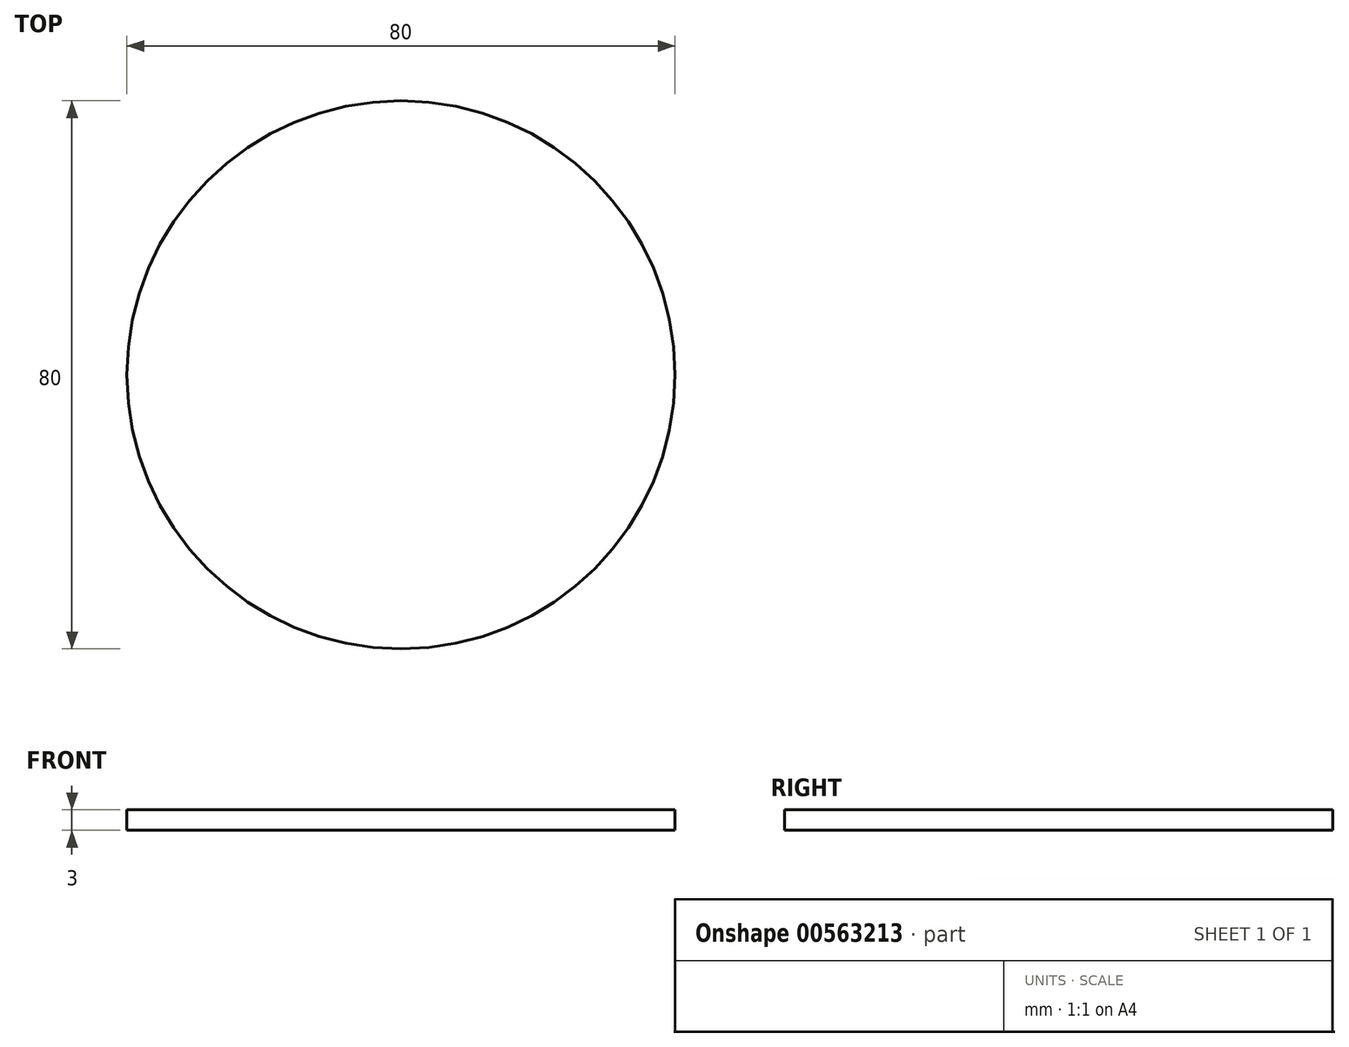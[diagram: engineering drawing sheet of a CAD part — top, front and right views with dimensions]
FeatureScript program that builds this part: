
annotation { "Feature Type Name" : "Feature", "Feature Type Description" : "" }
export const myFeature = defineFeature(function(context is Context, id is Id, definition is map)
    precondition{}
    {
        {
            var Q0;
            Q0=qCreatedBy(makeId("Top.planeOp"),FACE);
            var sketch = newSketch(context, id + "F0", { "sketchPlane" : qUnion([Q0])});
            skCircle(sketch, "E0", {"center": v(0, 0) * mm, "radius": 40 * mm});
            skSolve(sketch);
        }
        {
            var Q0;
            Q0=qSketchRegion(id+"F0",true);
            extrude(context, id + "F1", {"entities" : qUnion([Q0]), "endBound" : BoundingType.SYMMETRIC, "depth" : 3 * mm, "offsetDistance" : 25 * mm});
        }
    });
